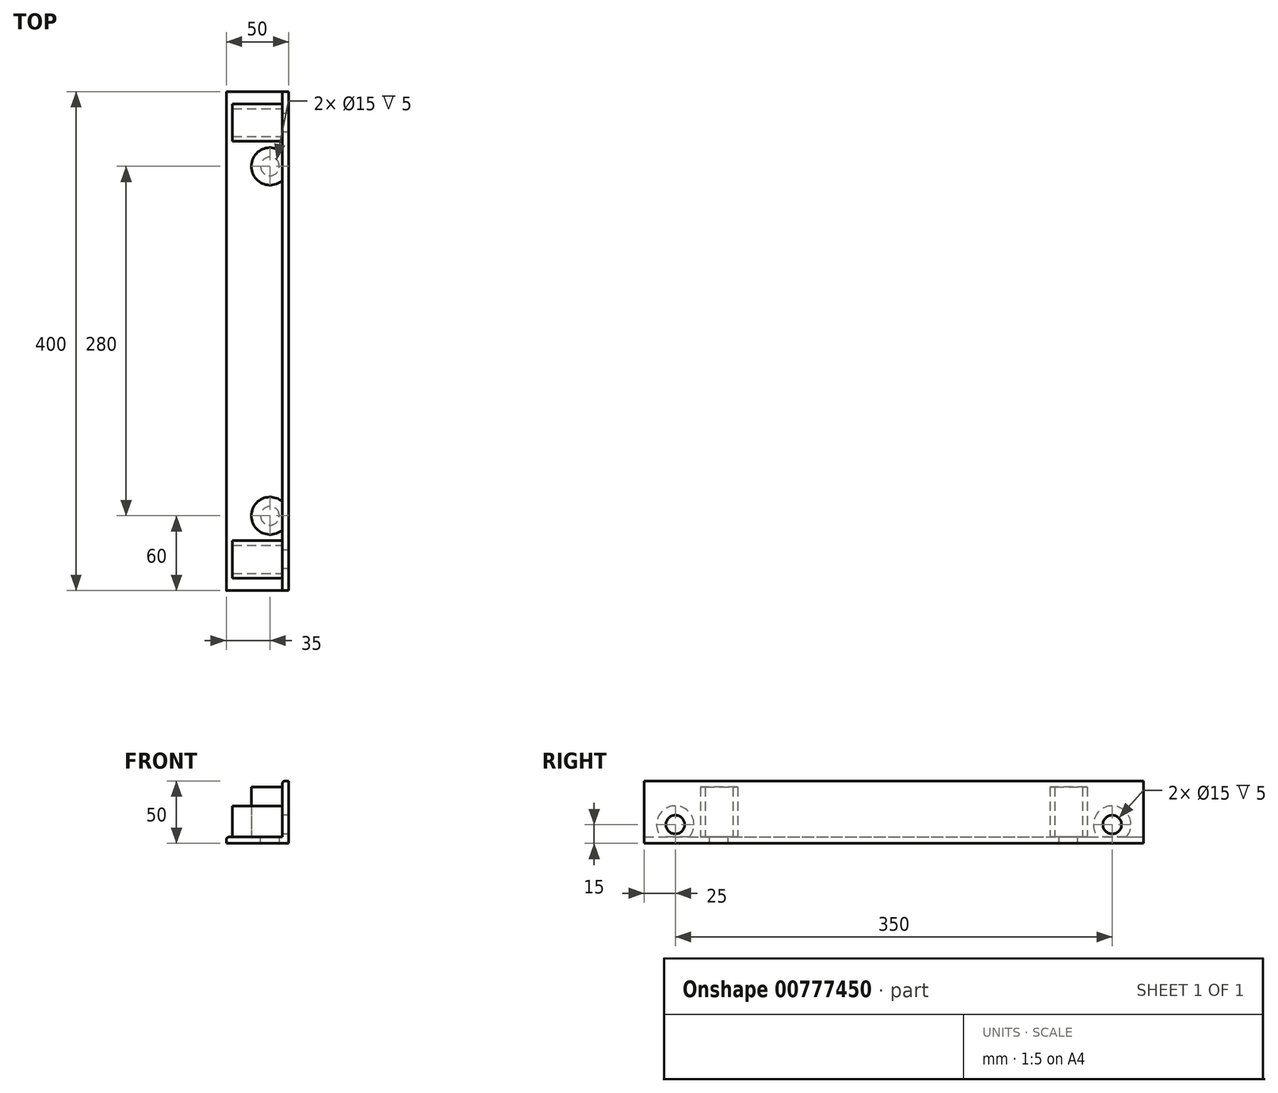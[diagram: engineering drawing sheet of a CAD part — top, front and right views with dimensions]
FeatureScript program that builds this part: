
annotation { "Feature Type Name" : "Feature", "Feature Type Description" : "" }
export const myFeature = defineFeature(function(context is Context, id is Id, definition is map)
    precondition{}
    {
        {
            var Q0;
            Q0=qCreatedBy(makeId("Front.planeOp"),FACE);
            var sketch = newSketch(context, id + "F0", { "sketchPlane" : qUnion([Q0])});
            skLineSegment(sketch, "E0", {"start": v(-3, 50) * mm, "end": v(0, 50) * mm});
            skLineSegment(sketch, "E1", {"start": v(0, 50) * mm, "end": v(0, 0) * mm});
            skLineSegment(sketch, "E2", {"start": v(0, 0) * mm, "end": v(-50, 0) * mm});
            skLineSegment(sketch, "E3", {"start": v(-50, 0) * mm, "end": v(-50, 3) * mm});
            skLineSegment(sketch, "E4", {"start": v(-48, 5) * mm, "end": v(-5, 5) * mm});
            skLineSegment(sketch, "E5", {"start": v(-5, 5) * mm, "end": v(-5, 48) * mm});
            skPoint(sketch, "E6.visualSharp", {"position": v(-5, 50) * mm});
            skArc(sketch, "E6.filletArc", {"start": v(-3, 50) * mm, "mid": v(-4.41, 49.41) * mm, "end": v(-5, 48) * mm});
            skPoint(sketch, "E7.visualSharp", {"position": v(-50, 5) * mm});
            skArc(sketch, "E7.filletArc", {"start": v(-48, 5) * mm, "mid": v(-49.41, 4.41) * mm, "end": v(-50, 3) * mm});
            skSolve(sketch);
        }
        {
            var Q0;
            Q0 = qSketchRegion(id + "F0", true);
            extrude(context, id + "F1", {"entities" : qUnion([Q0]), "depth" : 400 * mm, "offsetDistance" : 25 * mm});
        }
        {
            var Q0;
            Q0=makeQuery(id+"F1.opExtrude","SWEPT_FACE",FACE,{"disambiguationData":[OSD([sQuery(id+"F0.wireOp",EDGE,"E5")])]});
            var sketch = newSketch(context, id + "F2", { "sketchPlane" : qUnion([Q0])});
            skCircle(sketch, "E8", {"center": v(25, 15) * mm, "radius": 7.5 * mm});
            skLineSegment(sketch, "E9", {"start": v(200, -11.82) * mm, "end": v(200, 63.75) * mm});
            skPoint(sketch, "E9.startSnap0", {"position": v(200, 5) * mm});
            skPoint(sketch, "E9.endSnap0", {"position": v(200, 48) * mm});
            skCircle(sketch, "E10.MirrorC", {"center": v(375, 15) * mm, "radius": 7.5 * mm});
            skSolve(sketch);
        }
        {
            var Q0;
            Q0 = qSketchRegion(id + "F2", true);
            extrude(context, id + "F3", {"entities" : qUnion([Q0]), "operationType" : NewBodyOperationType.REMOVE, "endBound" : BoundingType.UP_TO_NEXT, "oppositeDirection" : true, "depth" : 25 * mm, "offsetDistance" : 25 * mm});
        }
        {
            var Q0;
            Q0=makeQuery(id+"F1.opExtrude","SWEPT_FACE",FACE,{"disambiguationData":[OSD([sQuery(id+"F0.wireOp",EDGE,"E4")])]});
            var sketch = newSketch(context, id + "F4", { "sketchPlane" : qUnion([Q0])});
            skCircle(sketch, "E11", {"center": v(-15, -60) * mm, "radius": 7.5 * mm});
            skLineSegment(sketch, "E12", {"start": v(-48, -200) * mm, "end": v(10.8, -200) * mm});
            skCircle(sketch, "E13.MirrorC", {"center": v(-15, -340) * mm, "radius": 7.5 * mm});
            skSolve(sketch);
        }
        {
            var Q0;
            Q0 = qSketchRegion(id + "F4", true);
            extrude(context, id + "F5", {"entities" : qUnion([Q0]), "operationType" : NewBodyOperationType.REMOVE, "endBound" : BoundingType.UP_TO_NEXT, "oppositeDirection" : true, "depth" : 25 * mm, "offsetDistance" : 25 * mm});
        }
        {
            var Q0;
            Q0=makeQuery(id+"F1.opExtrude","SWEPT_FACE",FACE,{"disambiguationData":[OSD([sQuery(id+"F0.wireOp",EDGE,"E5")])]});
            var sketch = newSketch(context, id + "F6", { "sketchPlane" : qUnion([Q0])});
            skCircle(sketch, "E14", {"center": v(375, 15) * mm, "radius": 15 * mm});
            skCircle(sketch, "E15", {"center": v(25, 15) * mm, "radius": 15 * mm});
            skSolve(sketch);
        }
        {
            var Q0;
            Q0 = qSketchRegion(id + "F6", true);
            extrude(context, id + "F7", {"entities" : qUnion([Q0]), "operationType" : NewBodyOperationType.ADD, "depth" : 40 * mm, "offsetDistance" : 25 * mm});
        }
        {
            var Q0;
            Q0=makeQuery(id+"F1.opExtrude","SWEPT_FACE",FACE,{"disambiguationData":[OSD([sQuery(id+"F0.wireOp",EDGE,"E4")])]});
            var sketch = newSketch(context, id + "F8", { "sketchPlane" : qUnion([Q0])});
            skCircle(sketch, "E16", {"center": v(-15, -340) * mm, "radius": 15 * mm});
            skCircle(sketch, "E17", {"center": v(-15, -60) * mm, "radius": 15 * mm});
            skSolve(sketch);
        }
        {
            var Q0;
            Q0 = qSketchRegion(id + "F8", true);
            extrude(context, id + "F9", {"entities" : qUnion([Q0]), "operationType" : NewBodyOperationType.ADD, "depth" : 40 * mm, "offsetDistance" : 25 * mm});
        }
    });
